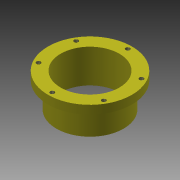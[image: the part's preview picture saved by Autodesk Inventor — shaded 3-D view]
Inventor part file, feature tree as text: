
AUTODESK INVENTOR PART (.ipt)
format: ipt  version: 2015 (Build 190159000, 159)  size: 553,472 bytes
history: native  units: in
note: dims shown in document units (in); Inventor stores cm internally (conversion verified against a paired STEP export)
features: thread x34, other x13, fillet x11, sketch x10, plane x6, projected_geometry x6, extrude x5, hole x4, mirror x3, pattern_circular x1, boolean_combine x1
ambient origin geometry x8: Origin, YZ Plane, XZ Plane, XY Plane, X Axis, Y Axis, Z Axis, Center Point
bodies: Solid6 (feature_tree)
feature tree (94):
  other  "board_with_hole_pipes.ipt"
  other  "Layout with const "
  plane  "Work Plane1"
  extrude  "Extrusion1"  Depth=18.0in
  extrude  "Extrusion2"  Depth=24.0in
  hole  "Hole1"  [1 undecoded]
  thread  "Thread1"  [1 undecoded]
  pattern_circular  "Circular Pattern1"  [2 undecoded]
  plane  "Work Plane3"
  hole  "Hole2"  [1 undecoded]
  thread  "Thread2"  [1 undecoded]
  thread  "Thread3"  [1 undecoded]
  thread  "Thread4"  [1 undecoded]
  thread  "Thread5"  [1 undecoded]
  thread  "Thread6"  [1 undecoded]
  thread  "Thread7"  [1 undecoded]
  mirror  "Mirror1"
  mirror  "Mirror2"
  mirror  "Mirror3"
  plane  "Work Plane4"
  extrude  "Extrusion3"  Depth=0.125in
  thread  "Thread8"  [1 undecoded]
  thread  "Thread9"  [1 undecoded]
  thread  "Thread10"  [1 undecoded]
  thread  "Thread11"  [1 undecoded]
  thread  "Thread12"  [1 undecoded]
  thread  "Thread13"  [1 undecoded]
  thread  "Thread14"  [1 undecoded]
  thread  "Thread15"  [1 undecoded]
  thread  "Thread16"  [1 undecoded]
  thread  "Thread17"  [1 undecoded]
  thread  "Thread18"  [1 undecoded]
  thread  "Thread19"  [1 undecoded]
  thread  "Thread20"  [1 undecoded]
  thread  "Thread21"  [1 undecoded]
  thread  "Thread22"  [1 undecoded]
  thread  "Thread23"  [1 undecoded]
  thread  "Thread24"  [1 undecoded]
  thread  "Thread25"  [1 undecoded]
  extrude  "Extrusion4"  Depth=1.0in TaperAngle=0.0deg
  plane  "Work Plane7"
  extrude  "Extrusion5"  Depth=1.0in TaperAngle=0.0deg
  boolean_combine  "Combine1"
  plane  "Work Plane8"
  plane  "Work Plane9"
  hole  "Hole3"  [1 undecoded]
  hole  "Hole4"  [1 undecoded]
  thread  "Thread26"  [1 undecoded]
  thread  "Thread27"  [1 undecoded]
  thread  "Thread28"  [1 undecoded]
  thread  "Thread29"  [1 undecoded]
  fillet  "Fillet2"  Radius=1.0in
  fillet  "Fillet3"  Radius=1.0in
  fillet  "Fillet4"  Radius=1.0in
  thread  "Thread34"  [1 undecoded]
  thread  "Thread35"  [1 undecoded]
  thread  "Thread36"  [1 undecoded]
  thread  "Thread37"  [1 undecoded]
  thread  "Thread38"  [1 undecoded]
  fillet  "Fillet5"  Radius=1.0in
  fillet  "Fillet6"  Radius=1.0in
  fillet  "Fillet7"  Radius=1.0in
  fillet  "Fillet8"  Radius=2.0in
  fillet  "Fillet9"  Radius=1.0in
  fillet  "Fillet10"  Radius=0.5in
  fillet  "Fillet11"  Radius=0.5in
  fillet  "Fillet12"  Radius=0.5in
  other  "Solid1::board_with_hole_pipes.ipt"
  other  "TaggingFeature1"
  sketch  "Sketch3"  dims[d0=0.1969in d1=18.0in]
  sketch  "Sketch4"  dims[d2=24.0in d3=23.5in]
  other  "legFL"
  sketch  "Sketch5"  dims[d4=17.5in d5=5.5in d6=1.5in]
  sketch  "Sketch6"  dims[d9=5.5in]
  sketch  "Sketch7"  dims[d10=1.5in]
  other  "Pattern of legFL:1"
  other  "legFR"
  other  "Pattern of legFL:2"
  other  "legBR"
  other  "Pattern of legFR:3"
  other  "legBL"
  sketch  "Sketch8"  dims[d11=5.5in]
  projected_geometry  "Projected Loop2"
  sketch  "Sketch10"  dims[d12=1.5in]
  sketch  "Sketch11"  dims[d15=4.0in]
  other  "miniplat"
  sketch  "Sketch12"  dims[d18=5.5in]
  projected_geometry  "Projected Loop3"
  projected_geometry  "Projected Loop4"
  projected_geometry  "Projected Loop5"
  projected_geometry  "Projected Loop6"
  projected_geometry  "Projected Loop7"
  sketch  "Sketch13"  dims[d19=1.5in d22=5.0in d23=3.0in d24=5.0in d25=3.0in d26=3.0in d27=3.0in d28=3.0in d29=5.0in d30=4.0in d31=3.5in d32=0.5in d33=1.0in d34=0.0in d35=0.0in d36=5.0in d37=0.5in d38=0.0in d39=0.25in d40=0.75in d41=0.375in d42=0.25in d43=0.5635in d44=1.8125in d45=0.8108in d46=1.0in d47=0.0in d48=2.3622in d49=360.0deg d52=0.25in d53=0.75in d54=0.375in d55=0.25in d56=0.5635in d57=1.8125in d58=0.8108in d59=1.0in d60=0.0in d61=1.0in d62=0.0in d63=1.0in d64=0.0in d65=1.0in d66=0.0in d67=1.0in d68=0.0in d69=1.0in d70=0.0in d71=3.475in d72=0.0in d73=1.0in d74=0.0in d75=1.0in d76=0.0in d77=1.0in d78=0.0in d79=1.0in d80=0.0in d81=1.0in d82=0.0in d83=1.0in d84=0.0in d85=1.0in d86=0.0in d87=1.0in d88=0.0in d89=1.0in d90=0.0in d91=1.0in d92=0.0in d93=1.0in d94=0.0in d95=1.0in d96=0.0in d97=1.0in d98=0.0in d99=1.0in d100=0.0in d101=1.0in d102=0.0in d103=1.0in d104=0.0in d105=1.0in d106=0.0in d107=1.0in d108=0.0in d109=1.0in d110=1.0in d111=1.0in d112=1.0in d113=1.0in d114=1.0in d115=2.0in d116=0.0in d117=1.0in d118=0.0in d119=0.5in d120=0.5in d121=0.5in d122=0.5in d123=0.25in d124=0.75in d125=0.375in d126=0.25in d127=0.5635in d128=2.0in d129=0.0in d130=0.5in d131=0.75in d132=0.375in d133=0.25in d134=0.5635in d135=2.0in d136=0.8108in d137=1.0in d138=0.0in d139=1.0in d140=0.0in d141=1.0in d142=0.0in d143=1.0in d144=0.0in d153=0.125in d154=0.125in d155=0.125in d156=1.0in d157=0.0in d158=1.0in d159=0.0in d160=1.0in d161=0.0in d162=1.0in d163=0.0in d164=1.0in d165=0.0in d166=0.125in d167=0.125in d168=0.125in d169=0.125in d170=0.125in d171=0.125in d172=0.125in d173=0.125in]
  other  "platform"
note: 40 required parameter values undecoded (feature->parameter linkage not recoverable at this tier; creation-order binding heuristic only, values carry confidence <= 0.55)
